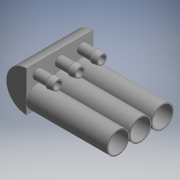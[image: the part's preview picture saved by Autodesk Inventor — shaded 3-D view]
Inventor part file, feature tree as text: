
AUTODESK INVENTOR PART (.ipt)
format: ipt  version: 2018 (Build 220112000, 112)  size: 384,000 bytes
history: native  units: in
note: dims shown in document units (in); Inventor stores cm internally (conversion verified against a paired STEP export)
features: other x10, extrude x5, sheet_metal_op x1, loft x1, fillet x1, pattern_linear x1, projected_geometry x1
ambient origin geometry x8: Origin, YZ Plane, XZ Plane, XY Plane, X Axis, Y Axis, Z Axis, Center Point
bodies: Body1 (feature_tree)
feature tree (20):
  sheet_metal_op  "Bend"
  extrude  "Convert to Whistle"  Depth=0.4331in
  loft  "Path to Slit"
  extrude  "Whistle Adapter"  Depth=0.1969in TaperAngle=0.0deg
  extrude  "Tube Segment"  TaperAngle=0.0deg  [1 undecoded]
  extrude  "Edge Cut"  TaperAngle=0.0deg  [1 undecoded]
  fillet  "Edge Fillet"  Radius=0.1969in
  extrude  "Whistle Tube Socket"  Depth=0.1969in
  other  "Silicone Fitting"
  pattern_linear  "Rectangular Pattern3"  Spacing1=0.0394in  [1 undecoded]
  other  "Bend Sketch"
  other  "Convert to Whistle Sketch"
  other  "Slit Sketch"
  other  "Edges3"
  other  "Whistle Adapter Profile Sketch"
  projected_geometry  "Projected Loop3"
  other  "Tube Segment Sketch"
  other  "Edge Cut Sketch"
  other  "Whistle Tube Socket Sketch"
  other  "Silicone Fitting Sketch"
note: 3 required parameter values undecoded (feature->parameter linkage not recoverable at this tier; creation-order binding heuristic only, values carry confidence <= 0.55)
